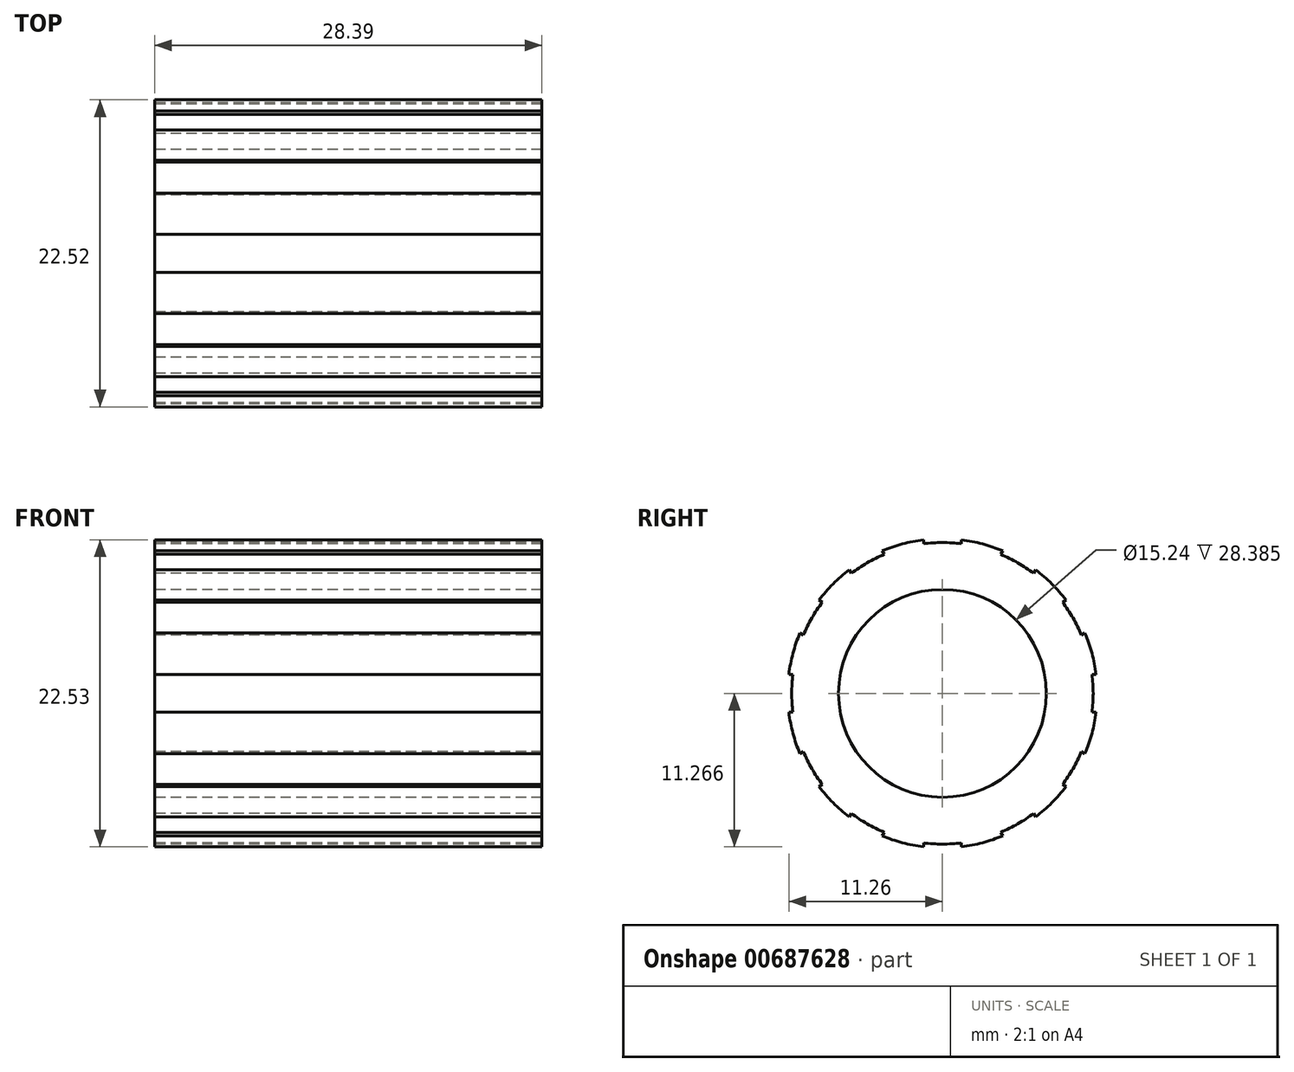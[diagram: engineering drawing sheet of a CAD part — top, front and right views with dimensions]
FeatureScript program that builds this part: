
annotation { "Feature Type Name" : "Feature", "Feature Type Description" : "" }
export const myFeature = defineFeature(function(context is Context, id is Id, definition is map)
    precondition{}
    {
        {
            var Q0;
            Q0=qCreatedBy(makeId("Front.planeOp"),FACE);
            var sketch = newSketch(context, id + "F0", { "sketchPlane" : qUnion([Q0])});
            skLineSegment(sketch, "E0.bottom", {"start": v(-192.06, -26.1) * mm, "end": v(-163.67, -26.1) * mm});
            skLineSegment(sketch, "E1", {"start": v(-192.06, -37.45) * mm, "end": v(-163.67, -37.45) * mm});
            skLineSegment(sketch, "E2", {"start": v(-192.06, -26.1) * mm, "end": v(-192.06, -37.45) * mm});
            skLineSegment(sketch, "E3", {"start": v(-192.06, -29.83) * mm, "end": v(-163.67, -29.83) * mm});
            skLineSegment(sketch, "E4", {"start": v(-163.67, -29.83) * mm, "end": v(-163.67, -26.1) * mm});
            skSolve(sketch);
        }
        {
            var Q0;
            {var subQ0=sQuery(id+"F0.wireOp",EDGE,"E0.bottom");Q0=makeQuery(id+"F0.imprint","IMPRINT",FACE,{"disambiguationData":[TD([[makeQuery(id+"F0.imprint","IMPRINT",EDGE,{"derivedFrom":subQ0}),-1.0]])]});}
            var Q1;
            Q1=sQuery(id+"F0.wireOp",EDGE,"E1");
            revolve(context, id + "F1", {"surfaceOperationType" : NewSurfaceOperationType.NEW, "entities" : qUnion([Q0]), "axis" : qUnion([Q1]), "revolveType" : RevolveType.FULL});
        }
        {
            var Q0;
            Q0=makeQuery(id+"F1.opRevolve","SWEPT_FACE",FACE,{"disambiguationData":[OSD([sQuery(id+"F0.wireOp",EDGE,"E2")])]});
            var sketch = newSketch(context, id + "F2", { "sketchPlane" : qUnion([Q0])});
            skArc(sketch, "E5.0", {"start": v(1.4, -26.2) * mm, "mid": v(0, -26.1) * mm, "end": v(-1.4, -26.2) * mm});
            skCircle(sketch, "E6.0", {"center": v(0, -37.45) * mm, "radius": 7.62 * mm});
            skLineSegment(sketch, "E7", {"start": v(0, -26.4) * mm, "end": v(0, -48.8) * mm, "construction": true});
            skArc(sketch, "E8", {"start": v(1.4, -26.49) * mm, "mid": v(0, -26.4) * mm, "end": v(-1.4, -26.49) * mm});
            skPoint(sketch, "E9", {"position": v(1.4, -26.49) * mm});
            skLineSegment(sketch, "E10", {"start": v(1.4, -26.49) * mm, "end": v(1.4, -26.2) * mm});
            skLineSegment(sketch, "E11.MirrorCS", {"start": v(-1.4, -26.49) * mm, "end": v(-1.4, -26.2) * mm});
            skPoint(sketch, "E12.start.orphan", {"position": v(0, -26.1) * mm});
            skSolve(sketch);
        }
        {
            var Q0;
            Q0=makeQuery(id+"F2.imprint","IMPRINT",FACE,{"disambiguationData":[TD([[makeQuery(id+"F2.imprint","IMPRINT",EDGE,{"derivedFrom":sQuery(id+"F2.wireOp",EDGE,"E5.0")}),1.0]])]});
            extrude(context, id + "F3", {"entities" : qUnion([Q0]), "operationType" : NewBodyOperationType.REMOVE, "endBound" : BoundingType.THROUGH_ALL, "oppositeDirection" : true, "depth" : 25.4 * mm, "offsetDistance" : 25.4 * mm});
        }
        {
            var Q0;
            Q0=makeQuery(id+"F3.boolean.opBoolean","COPY",FACE,{"derivedFrom":makeQuery(id+"F3.opExtrude","SWEPT_FACE",FACE,{"disambiguationData":[OSD([sQuery(id+"F2.wireOp",EDGE,"E11.MirrorCS")])]})});
            var Q1;
            Q1=makeQuery(id+"F3.boolean.opBoolean","COPY",FACE,{"derivedFrom":makeQuery(id+"F3.opExtrude","SWEPT_FACE",FACE,{"disambiguationData":[OSD([sQuery(id+"F2.wireOp",EDGE,"E10")])]})});
            var Q2;
            Q2=makeQuery(id+"F3.boolean.opBoolean","COPY",FACE,{"derivedFrom":makeQuery(id+"F3.opExtrude","SWEPT_FACE",FACE,{"disambiguationData":[OSD([sQuery(id+"F2.wireOp",EDGE,"E8")])]})});
            var Q3;
            Q3=makeQuery(id+"F1.opRevolve","SWEPT_FACE",FACE,{"disambiguationData":[OSD([sQuery(id+"F0.wireOp",EDGE,"E0.bottom")])]});
            circularPattern(context, id + "F4", {"patternType" : PatternType.FACE, "faces" : qUnion([Q0, Q1, Q2]), "axis" : qUnion([Q3]), "angle" : 360 * degree, "instanceCount" : 12, "equalSpace" : true});
        }
    });
